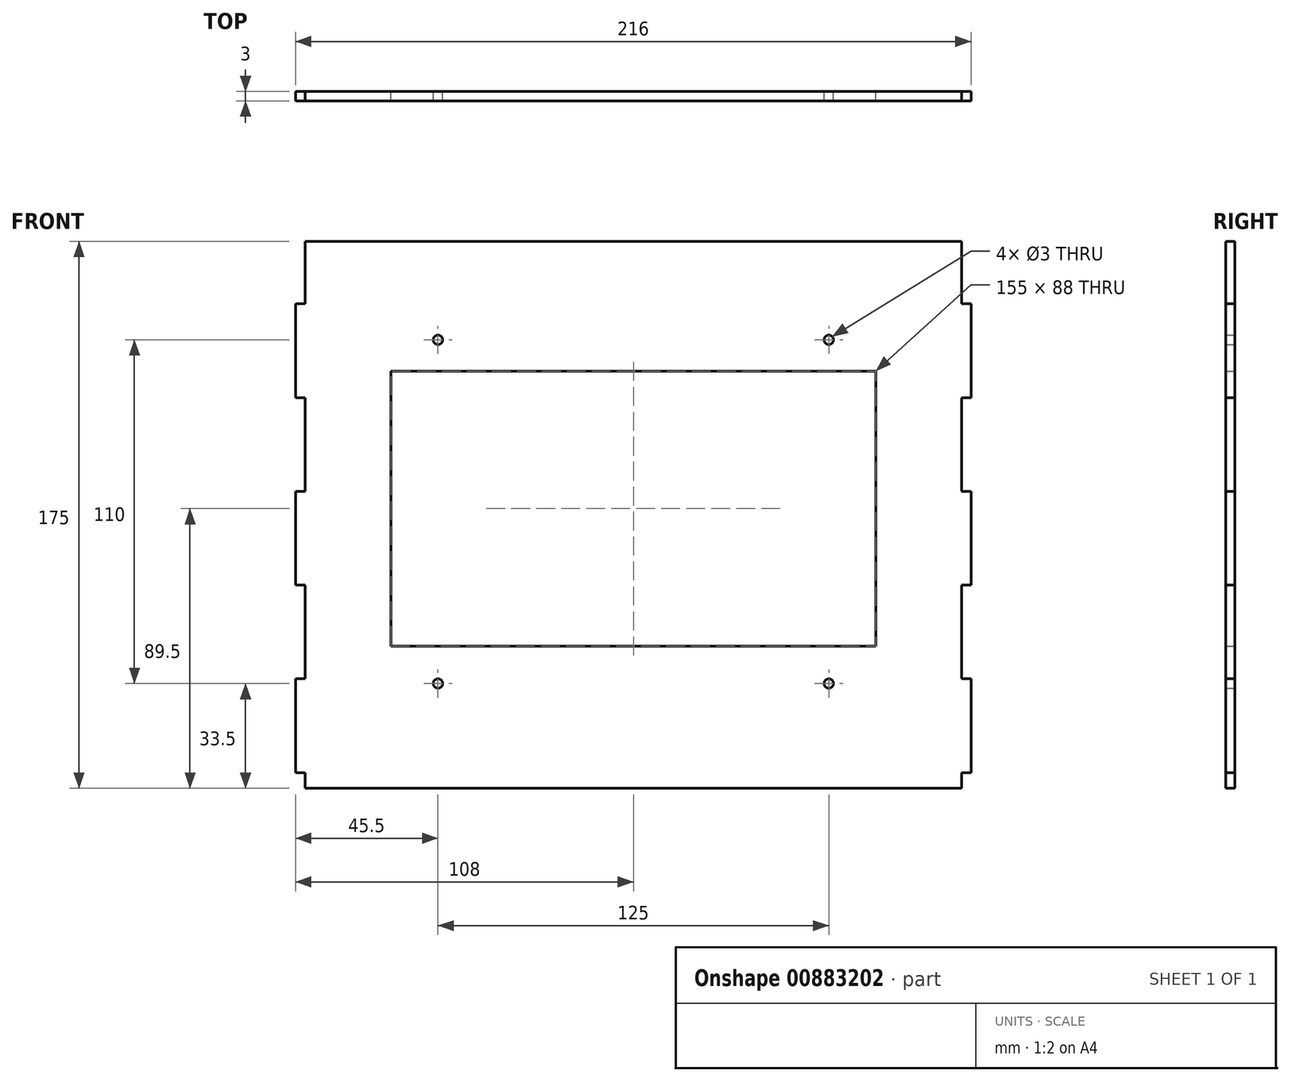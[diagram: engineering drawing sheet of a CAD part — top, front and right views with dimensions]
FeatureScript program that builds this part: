
annotation { "Feature Type Name" : "Feature", "Feature Type Description" : "" }
export const myFeature = defineFeature(function(context is Context, id is Id, definition is map)
    precondition{}
    {
        {
            var Q0;
            Q0=qCreatedBy(makeId("Front.planeOp"),FACE);
            var sketch = newSketch(context, id + "F0", { "sketchPlane" : qUnion([Q0])});
            skLineSegment(sketch, "E0.bottom", {"start": v(105, 87.5) * mm, "end": v(-105, 87.5) * mm});
            skLineSegment(sketch, "E0.top", {"start": v(105, -87.5) * mm, "end": v(-105, -87.5) * mm});
            skLineSegment(sketch, "E0.left", {"start": v(105, 87.5) * mm, "end": v(105, -87.5) * mm});
            skLineSegment(sketch, "E0.right", {"start": v(-105, 87.5) * mm, "end": v(-105, -87.5) * mm});
            skPoint(sketch, "E0.middle", {"position": v(0, 0) * mm});
            skLineSegment(sketch, "E1.bottom", {"start": v(77.5, 46) * mm, "end": v(-77.5, 46) * mm});
            skLineSegment(sketch, "E1.top", {"start": v(77.5, -42) * mm, "end": v(-77.5, -42) * mm});
            skLineSegment(sketch, "E1.left", {"start": v(77.5, 46) * mm, "end": v(77.5, -42) * mm});
            skLineSegment(sketch, "E1.right", {"start": v(-77.5, 46) * mm, "end": v(-77.5, -42) * mm});
            skPoint(sketch, "E1.middle", {"position": v(0, 2) * mm});
            skCircle(sketch, "E2", {"center": v(62.5, 56) * mm, "radius": 1.5 * mm});
            skCircle(sketch, "E3.0.1.0", {"center": v(62.5, -54) * mm, "radius": 1.5 * mm});
            skLineSegment(sketch, "E4", {"start": v(105, 67.5) * mm, "end": v(108, 67.5) * mm});
            skLineSegment(sketch, "E5", {"start": v(108, 67.5) * mm, "end": v(108, 37.5) * mm});
            skLineSegment(sketch, "E6", {"start": v(108, 37.5) * mm, "end": v(105, 37.5) * mm});
            skLineSegment(sketch, "E7", {"start": v(105, -52.5) * mm, "end": v(108, -52.5) * mm});
            skLineSegment(sketch, "E8", {"start": v(108, -52.5) * mm, "end": v(108, -82.5) * mm});
            skLineSegment(sketch, "E9", {"start": v(108, -82.5) * mm, "end": v(105, -82.5) * mm});
            skLineSegment(sketch, "E10", {"start": v(105, 7.5) * mm, "end": v(108, 7.5) * mm});
            skLineSegment(sketch, "E11", {"start": v(108, 7.5) * mm, "end": v(108, -22.5) * mm});
            skLineSegment(sketch, "E12", {"start": v(108, -22.5) * mm, "end": v(105, -22.5) * mm});
            skLineSegment(sketch, "E13", {"start": v(0, 87.5) * mm, "end": v(0, -87.5) * mm, "construction": true});
            skLineSegment(sketch, "E14.MirrorCS", {"start": v(-105, 67.5) * mm, "end": v(-108, 67.5) * mm});
            skLineSegment(sketch, "E15.MirrorCS", {"start": v(-108, 67.5) * mm, "end": v(-108, 37.5) * mm});
            skLineSegment(sketch, "E16.MirrorCS", {"start": v(-108, 37.5) * mm, "end": v(-105, 37.5) * mm});
            skLineSegment(sketch, "E17.MirrorCS", {"start": v(-105, 7.5) * mm, "end": v(-108, 7.5) * mm});
            skLineSegment(sketch, "E18.MirrorCS", {"start": v(-108, 7.5) * mm, "end": v(-108, -22.5) * mm});
            skLineSegment(sketch, "E19.MirrorCS", {"start": v(-108, -22.5) * mm, "end": v(-105, -22.5) * mm});
            skLineSegment(sketch, "E20.MirrorCS", {"start": v(-105, -52.5) * mm, "end": v(-108, -52.5) * mm});
            skLineSegment(sketch, "E21.MirrorCS", {"start": v(-108, -52.5) * mm, "end": v(-108, -82.5) * mm});
            skLineSegment(sketch, "E22.MirrorCS", {"start": v(-108, -82.5) * mm, "end": v(-105, -82.5) * mm});
            skCircle(sketch, "E23.MirrorC", {"center": v(-62.5, 56) * mm, "radius": 1.5 * mm});
            skCircle(sketch, "E24.MirrorC", {"center": v(-62.5, -54) * mm, "radius": 1.5 * mm});
            skSolve(sketch);
        }
        {
            var Q0;
            Q0 = qSketchRegion(id + "F0", true);
            extrude(context, id + "F1", {"entities" : qUnion([Q0]), "depth" : 3 * mm, "offsetDistance" : 25 * mm});
        }
    });
